# Revit family: IS_Ceraplus_A4844_BIM_DE
name_source: partatom
category: Plumbing Fixtures
revit_build: Autodesk Revit MEP 2015 (Build: 20140606_1530(x64)
units: mm (PartAtom-declared; Revit-internal decimal feet)

## types (1)
- A4844AA - IS Kopfbrause CERAPLUS, vandalensicher, Ausld. 77mm, Chrom
    Assembly Code = C1030200
    BIMobject category = Showers
    BOSUseNativeGeometries = 1
    Brand url = http://www.idealstandard.co.uk
    Description = A4844AA CERAPLUS anti vandal fixed shower head
    EAN code = https://4015413325905
    Edition number = 1
    FaucetType = pillar
    FlushRate = 0 m³
    FlushingRate = 0
    IFC Classification = Valve
    IfcExportAs = IfcValveType
    IfcExportType = BRASSWARE SHOWER
    Installation instructions = http://www.idealstandard.cz
    Manufacturer name = Ideal Standard
    ManufacturerURL = www.idealstandard.com
    Material = Brass
    Material main = Brassware
    Model = A4844AA
    ModelNumber = A4844AA
    NBS Reference Code = 35-06-80
    NBS Reference Description = Shower Fittings Packages
    Name = CERAPLUS anti vandal fixed shower head
    NettWeight = 1,091 kg
    Nominal height = 81
    Nominal width = 67
    NominalDepth = 0 mm  [stored 0 ft]
    NominalHeight = 81 mm  [stored 0.265748 ft]
    NominalLength = 0 mm  [stored 0 ft]
    NominalWidth = 67 mm  [stored 0.219816 ft]
    OmniClass Code = 23.45.55.14
    OmniClass Description = Single Faucets
    Product Guid = 810eecad-b877-42c5-871d-986c97c0e506
    Product SKU = A4844
    Product data url = https://bimobject.com
    Product family = Sanitary
    Product group = Shower fittings package
    Product name = Ceraplus Head Shower Antivandal
    Product url = www.idealstandard.de/produkte
    ProductInformation = www.idealstandard.de/produkte
    QR code = http://bimobject.com
    Shape = Sculptured
    Space = Internal
    SpareParts = www.idealstandard.de/ersatzteile
    Technical description = www.idealstandard.de/produkte
    URL = www.idealstandard.com
    Uniclass 2.0 Code = PR-35-06-80
    Uniclass 2.0 Description = Shower Fittings Packages
    Uniclass 2015 Code = Pr_40_20_87_75
    Uniclass 2015 Name = Shower fittings package
    Version = 1
    VolumeUnits = Litres
    WarrantyDurationParts = 5
    WarrantyDurationUnit = year
    Weight Net (Kg) = 1.091
    WorkingPressure = 1-5 Bar

note: [stored X ft] marks values corroborated as IEEE doubles in the binary element streams (Revit-internal decimal feet)

## geometry (parser evidence)
native form markers: Blend x4, Sweep x1
no freeform markers — native parametric forms only
